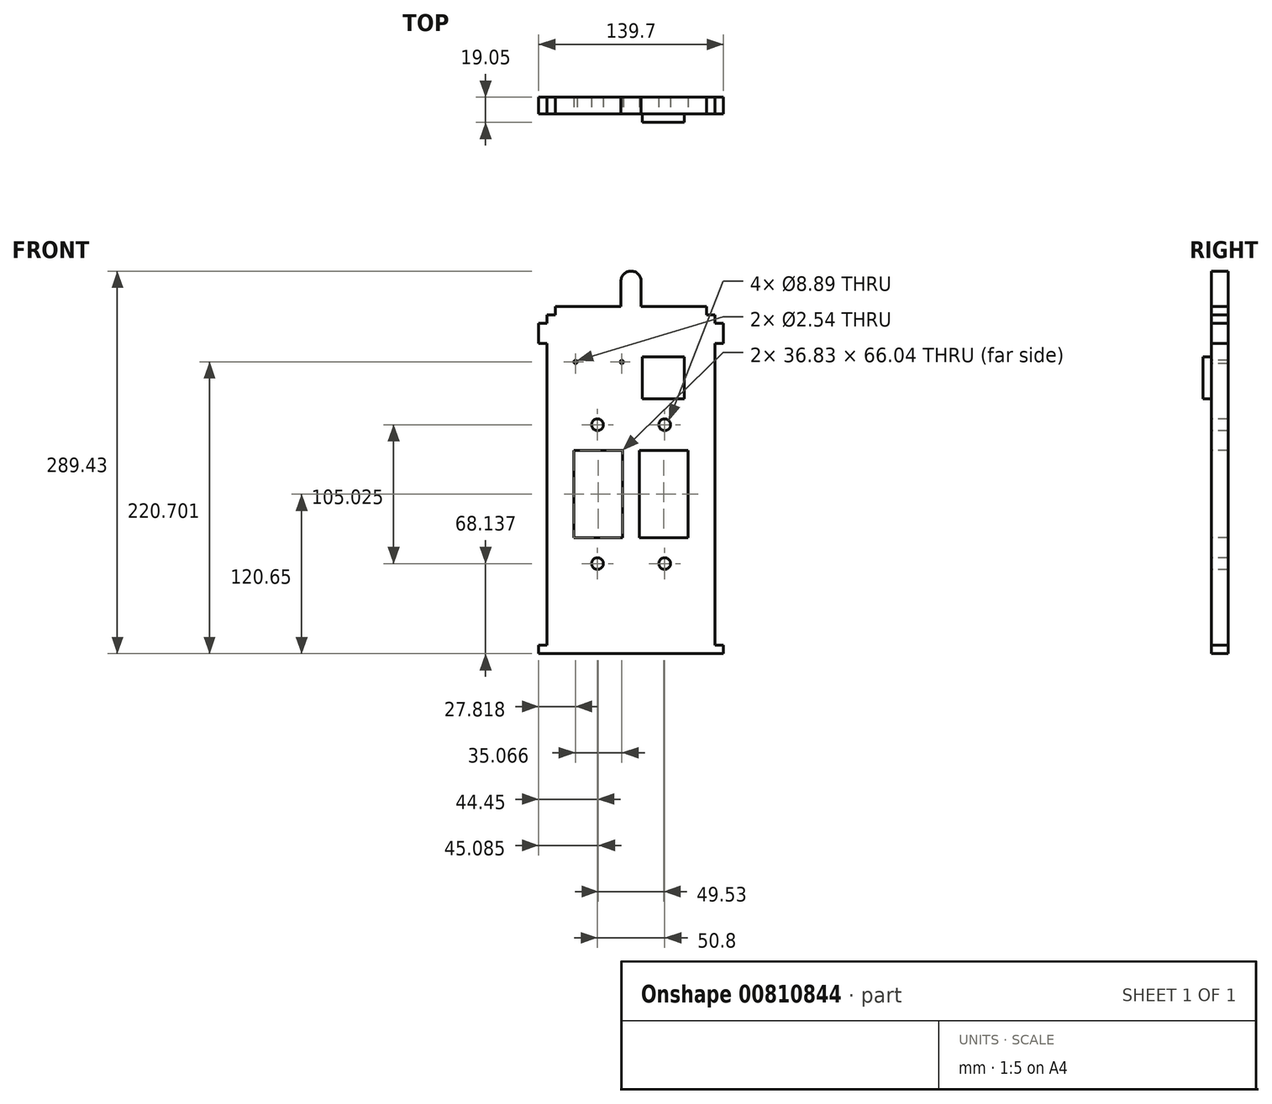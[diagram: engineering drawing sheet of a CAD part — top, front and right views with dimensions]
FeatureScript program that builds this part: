
annotation { "Feature Type Name" : "Feature", "Feature Type Description" : "" }
export const myFeature = defineFeature(function(context is Context, id is Id, definition is map)
    precondition{}
    {
        {
            var Q0;
            Q0=qCreatedBy(makeId("Front.planeOp"),FACE);
            var sketch = newSketch(context, id + "F0", { "sketchPlane" : qUnion([Q0])});
            skLineSegment(sketch, "E0.bottom", {"start": v(-63.5, 114.3) * mm, "end": v(63.5, 114.3) * mm});
            skLineSegment(sketch, "E0.top", {"start": v(-63.5, -114.3) * mm, "end": v(63.5, -114.3) * mm});
            skLineSegment(sketch, "E0.left", {"start": v(-63.5, 114.3) * mm, "end": v(-63.5, -114.3) * mm});
            skLineSegment(sketch, "E0.right", {"start": v(63.5, 114.3) * mm, "end": v(63.5, -114.3) * mm});
            skPoint(sketch, "E0.middle", {"position": v(0, 0) * mm});
            skLineSegment(sketch, "E1.bottom", {"start": v(-69.85, -114.3) * mm, "end": v(69.85, -114.3) * mm});
            skLineSegment(sketch, "E1.top", {"start": v(-69.85, -120.65) * mm, "end": v(69.85, -120.65) * mm});
            skLineSegment(sketch, "E1.left", {"start": v(-69.85, -114.3) * mm, "end": v(-69.85, -120.65) * mm});
            skLineSegment(sketch, "E1.right", {"start": v(69.85, -114.3) * mm, "end": v(69.85, -120.65) * mm});
            skPoint(sketch, "E1.middle", {"position": v(0, -117.47) * mm});
            skLineSegment(sketch, "E2.bottom", {"start": v(-69.85, 114.17) * mm, "end": v(69.85, 114.17) * mm});
            skLineSegment(sketch, "E2.top", {"start": v(-69.85, 129.41) * mm, "end": v(69.85, 129.41) * mm});
            skLineSegment(sketch, "E2.left", {"start": v(-69.85, 114.17) * mm, "end": v(-69.85, 129.41) * mm});
            skLineSegment(sketch, "E2.right", {"start": v(69.85, 114.17) * mm, "end": v(69.85, 129.41) * mm});
            skPoint(sketch, "E2.middle", {"position": v(0, 121.8) * mm});
            skPoint(sketch, "E3", {"position": v(0, 114.3) * mm});
            skLineSegment(sketch, "E4.bottom", {"start": v(-63.5, 129.41) * mm, "end": v(63.5, 129.41) * mm});
            skLineSegment(sketch, "E4.top", {"start": v(-63.5, 135.76) * mm, "end": v(63.5, 135.76) * mm});
            skLineSegment(sketch, "E4.left", {"start": v(-63.5, 129.41) * mm, "end": v(-63.5, 135.76) * mm});
            skLineSegment(sketch, "E4.right", {"start": v(63.5, 129.41) * mm, "end": v(63.5, 135.76) * mm});
            skPoint(sketch, "E4.middle", {"position": v(0, 132.59) * mm});
            skLineSegment(sketch, "E5.bottom", {"start": v(-57.15, 135.76) * mm, "end": v(57.15, 135.76) * mm});
            skLineSegment(sketch, "E5.top", {"start": v(-57.15, 142.11) * mm, "end": v(57.15, 142.11) * mm});
            skLineSegment(sketch, "E5.left", {"start": v(-57.15, 135.76) * mm, "end": v(-57.15, 142.11) * mm});
            skLineSegment(sketch, "E5.right", {"start": v(57.15, 135.76) * mm, "end": v(57.15, 142.11) * mm});
            skPoint(sketch, "E5.middle", {"position": v(0, 138.94) * mm});
            skPoint(sketch, "E5.middle.positionSnap0", {"position": v(0, 135.76) * mm});
            skPoint(sketch, "E5.centerSnap0", {"position": v(0, 135.76) * mm});
            skLineSegment(sketch, "E6.bottom", {"start": v(-7.62, 161.16) * mm, "end": v(7.62, 161.16) * mm});
            skLineSegment(sketch, "E6.top", {"start": v(-7.62, 142.11) * mm, "end": v(7.62, 142.11) * mm});
            skLineSegment(sketch, "E6.left", {"start": v(-7.62, 161.16) * mm, "end": v(-7.62, 142.11) * mm});
            skLineSegment(sketch, "E6.right", {"start": v(7.62, 161.16) * mm, "end": v(7.62, 142.11) * mm});
            skPoint(sketch, "E6.middle", {"position": v(0, 151.64) * mm});
            skArc(sketch, "E7", {"start": v(7.62, 161.16) * mm, "mid": v(0, 168.78) * mm, "end": v(-7.62, 161.16) * mm});
            skPoint(sketch, "E8", {"position": v(0, 142.11) * mm});
            skSolve(sketch);
        }
        {
            var Q0;
            Q0=makeQuery(id+"F0.imprint","IMPRINT",FACE,{"disambiguationData":[TD([[makeQuery(id+"F0.imprint","IMPRINT",EDGE,{"derivedFrom":sQuery(id+"F0.wireOp",EDGE,"E0.bottom")}),-1.0]])]});
            var sketch = newSketch(context, id + "F1", { "sketchPlane" : qUnion([Q0])});
            skPoint(sketch, "E9.middle", {"position": v(0, 0) * mm});
            skLineSegment(sketch, "E10", {"start": v(0, 114.31) * mm, "end": v(0, -114.28) * mm});
            skLineSegment(sketch, "E11.bottom", {"start": v(-63.5, 63.5) * mm, "end": v(63.5, 63.5) * mm});
            skLineSegment(sketch, "E11.top", {"start": v(-63.5, -63.5) * mm, "end": v(63.5, -63.5) * mm});
            skLineSegment(sketch, "E11.left", {"start": v(-63.5, 63.5) * mm, "end": v(-63.5, -63.5) * mm});
            skLineSegment(sketch, "E11.right", {"start": v(63.5, 63.5) * mm, "end": v(63.5, -63.5) * mm});
            skSolve(sketch);
        }
        {
            var Q0;
            Q0=makeQuery(id+"F0.imprint","IMPRINT",FACE,{"disambiguationData":[TD([[makeQuery(id+"F0.imprint","IMPRINT",EDGE,{"derivedFrom":sQuery(id+"F0.wireOp",EDGE,"E0.bottom")}),-1.0]])]});
            var sketch = newSketch(context, id + "F2", { "sketchPlane" : qUnion([Q0])});
            skLineSegment(sketch, "E12.bottom", {"start": v(8.4, 103.8) * mm, "end": v(40.16, 103.8) * mm});
            skLineSegment(sketch, "E12.top", {"start": v(8.4, 72.04) * mm, "end": v(40.16, 72.04) * mm});
            skLineSegment(sketch, "E12.left", {"start": v(8.4, 103.8) * mm, "end": v(8.4, 72.04) * mm});
            skLineSegment(sketch, "E12.right", {"start": v(40.16, 103.8) * mm, "end": v(40.16, 72.04) * mm});
            skPoint(sketch, "E12.middle", {"position": v(24.28, 87.92) * mm});
            skLineSegment(sketch, "E13.MirrorCS", {"start": v(-8.4, 103.8) * mm, "end": v(-40.16, 103.8) * mm, "construction": true});
            skLineSegment(sketch, "E14.MirrorCS", {"start": v(-8.4, 103.8) * mm, "end": v(-8.4, 72.04) * mm, "construction": true});
            skLineSegment(sketch, "E15.MirrorCS", {"start": v(-8.4, 72.04) * mm, "end": v(-40.16, 72.04) * mm, "construction": true});
            skLineSegment(sketch, "E16.MirrorCS", {"start": v(-40.16, 103.8) * mm, "end": v(-40.16, 72.04) * mm, "construction": true});
            skSolve(sketch);
        }
        {
            var Q0;
            Q0 = qSketchRegion(id + "F0", true);
            extrude(context, id + "F3", {"entities" : qUnion([Q0]), "endBound" : BoundingType.SYMMETRIC, "depth" : 12.7 * mm, "offsetDistance" : 25.4 * mm});
        }
        {
            var Q0;
            Q0 = qSketchRegion(id + "F2", true);
            extrude(context, id + "F4", {"entities" : qUnion([Q0]), "operationType" : NewBodyOperationType.ADD, "depth" : 12.7 * mm, "offsetDistance" : 25.4 * mm});
        }
        {
            var Q0;
            Q0=makeQuery(id+"F3.opExtrude","CAP_FACE",FACE,{"disambiguationData":[OSD([sQuery(id+"F0.wireOp",EDGE,"E0.left"),sQuery(id+"F0.wireOp",EDGE,"E0.right"),sQuery(id+"F0.wireOp",EDGE,"E1.bottom"),sQuery(id+"F0.wireOp",EDGE,"E1.top"),sQuery(id+"F0.wireOp",EDGE,"E1.left"),sQuery(id+"F0.wireOp",EDGE,"E1.right"),sQuery(id+"F0.wireOp",EDGE,"E2.bottom"),sQuery(id+"F0.wireOp",EDGE,"E2.top"),sQuery(id+"F0.wireOp",EDGE,"E2.left"),sQuery(id+"F0.wireOp",EDGE,"E2.right"),sQuery(id+"F0.wireOp",EDGE,"E4.top"),sQuery(id+"F0.wireOp",EDGE,"E4.left"),sQuery(id+"F0.wireOp",EDGE,"E4.right"),sQuery(id+"F0.wireOp",EDGE,"E5.top"),sQuery(id+"F0.wireOp",EDGE,"E5.left"),sQuery(id+"F0.wireOp",EDGE,"E5.right"),sQuery(id+"F0.wireOp",EDGE,"E6.left"),sQuery(id+"F0.wireOp",EDGE,"E6.right"),sQuery(id+"F0.wireOp",EDGE,"E7")])],"isStart":false});
            var sketch = newSketch(context, id + "F5", { "sketchPlane" : qUnion([Q0])});
            skLineSegment(sketch, "E17", {"start": v(6.35, -33.02) * mm, "end": v(6.35, 33.02) * mm});
            skLineSegment(sketch, "E18", {"start": v(6.35, 33.02) * mm, "end": v(43.18, 33.02) * mm});
            skLineSegment(sketch, "E19", {"start": v(43.18, 33.02) * mm, "end": v(43.18, -33.02) * mm});
            skLineSegment(sketch, "E20", {"start": v(43.18, -33.02) * mm, "end": v(6.35, -33.02) * mm});
            skLineSegment(sketch, "E21", {"start": v(-43.18, -33.02) * mm, "end": v(-6.35, -33.02) * mm});
            skLineSegment(sketch, "E22", {"start": v(-6.35, -33.02) * mm, "end": v(-6.35, 33.02) * mm});
            skLineSegment(sketch, "E23", {"start": v(-6.35, 33.02) * mm, "end": v(-43.18, 33.02) * mm});
            skLineSegment(sketch, "E24", {"start": v(-43.18, 33.02) * mm, "end": v(-43.18, -33.02) * mm});
            skSolve(sketch);
        }
        {
            var Q0;
            Q0 = qSketchRegion(id + "F5", true);
            extrude(context, id + "F6", {"entities" : qUnion([Q0]), "operationType" : NewBodyOperationType.REMOVE, "oppositeDirection" : true, "depth" : 50.8 * mm, "offsetDistance" : 25.4 * mm});
        }
        {
            var Q0;
            Q0=makeQuery(id+"F3.opExtrude","CAP_FACE",FACE,{"disambiguationData":[OSD([sQuery(id+"F0.wireOp",EDGE,"E0.left"),sQuery(id+"F0.wireOp",EDGE,"E0.right"),sQuery(id+"F0.wireOp",EDGE,"E1.bottom"),sQuery(id+"F0.wireOp",EDGE,"E1.top"),sQuery(id+"F0.wireOp",EDGE,"E1.left"),sQuery(id+"F0.wireOp",EDGE,"E1.right"),sQuery(id+"F0.wireOp",EDGE,"E2.bottom"),sQuery(id+"F0.wireOp",EDGE,"E2.top"),sQuery(id+"F0.wireOp",EDGE,"E2.left"),sQuery(id+"F0.wireOp",EDGE,"E2.right"),sQuery(id+"F0.wireOp",EDGE,"E4.top"),sQuery(id+"F0.wireOp",EDGE,"E4.left"),sQuery(id+"F0.wireOp",EDGE,"E4.right"),sQuery(id+"F0.wireOp",EDGE,"E5.top"),sQuery(id+"F0.wireOp",EDGE,"E5.left"),sQuery(id+"F0.wireOp",EDGE,"E5.right"),sQuery(id+"F0.wireOp",EDGE,"E6.left"),sQuery(id+"F0.wireOp",EDGE,"E6.right"),sQuery(id+"F0.wireOp",EDGE,"E7")])],"isStart":false});
            var sketch = newSketch(context, id + "F7", { "sketchPlane" : qUnion([Q0])});
            skCircle(sketch, "E25", {"center": v(-42.03, 100.05) * mm, "radius": 1.27 * mm});
            skCircle(sketch, "E26", {"center": v(-6.97, 100.05) * mm, "radius": 1.27 * mm});
            skSolve(sketch);
        }
        {
            var Q0;
            Q0 = qSketchRegion(id + "F7", true);
            extrude(context, id + "F8", {"entities" : qUnion([Q0]), "operationType" : NewBodyOperationType.REMOVE, "endBound" : BoundingType.SYMMETRIC, "oppositeDirection" : true, "depth" : 25.4 * mm, "offsetDistance" : 25.4 * mm});
        }
        {
            var Q0;
            Q0=makeQuery(id+"F3.opExtrude","CAP_FACE",FACE,{"disambiguationData":[OSD([sQuery(id+"F0.wireOp",EDGE,"E0.left"),sQuery(id+"F0.wireOp",EDGE,"E0.right"),sQuery(id+"F0.wireOp",EDGE,"E1.bottom"),sQuery(id+"F0.wireOp",EDGE,"E1.top"),sQuery(id+"F0.wireOp",EDGE,"E1.left"),sQuery(id+"F0.wireOp",EDGE,"E1.right"),sQuery(id+"F0.wireOp",EDGE,"E2.bottom"),sQuery(id+"F0.wireOp",EDGE,"E2.top"),sQuery(id+"F0.wireOp",EDGE,"E2.left"),sQuery(id+"F0.wireOp",EDGE,"E2.right"),sQuery(id+"F0.wireOp",EDGE,"E4.top"),sQuery(id+"F0.wireOp",EDGE,"E4.left"),sQuery(id+"F0.wireOp",EDGE,"E4.right"),sQuery(id+"F0.wireOp",EDGE,"E5.top"),sQuery(id+"F0.wireOp",EDGE,"E5.left"),sQuery(id+"F0.wireOp",EDGE,"E5.right"),sQuery(id+"F0.wireOp",EDGE,"E6.left"),sQuery(id+"F0.wireOp",EDGE,"E6.right"),sQuery(id+"F0.wireOp",EDGE,"E7")])],"isStart":false});
            var sketch = newSketch(context, id + "F9", { "sketchPlane" : qUnion([Q0])});
            skCircle(sketch, "E27", {"center": v(-25.4, 52.51) * mm, "radius": 4.45 * mm});
            skCircle(sketch, "E28.MirrorC", {"center": v(25.4, 52.51) * mm, "radius": 4.45 * mm});
            skCircle(sketch, "E29.MirrorC", {"center": v(-25.4, -52.51) * mm, "radius": 4.45 * mm});
            skCircle(sketch, "E30.MirrorC", {"center": v(25.4, -52.51) * mm, "radius": 4.45 * mm});
            skSolve(sketch);
        }
        {
            var Q0;
            Q0 = qSketchRegion(id + "F9", true);
            extrude(context, id + "F10", {"entities" : qUnion([Q0]), "operationType" : NewBodyOperationType.REMOVE, "endBound" : BoundingType.SYMMETRIC, "oppositeDirection" : true, "depth" : 25.4 * mm, "offsetDistance" : 25.4 * mm});
        }
    });
